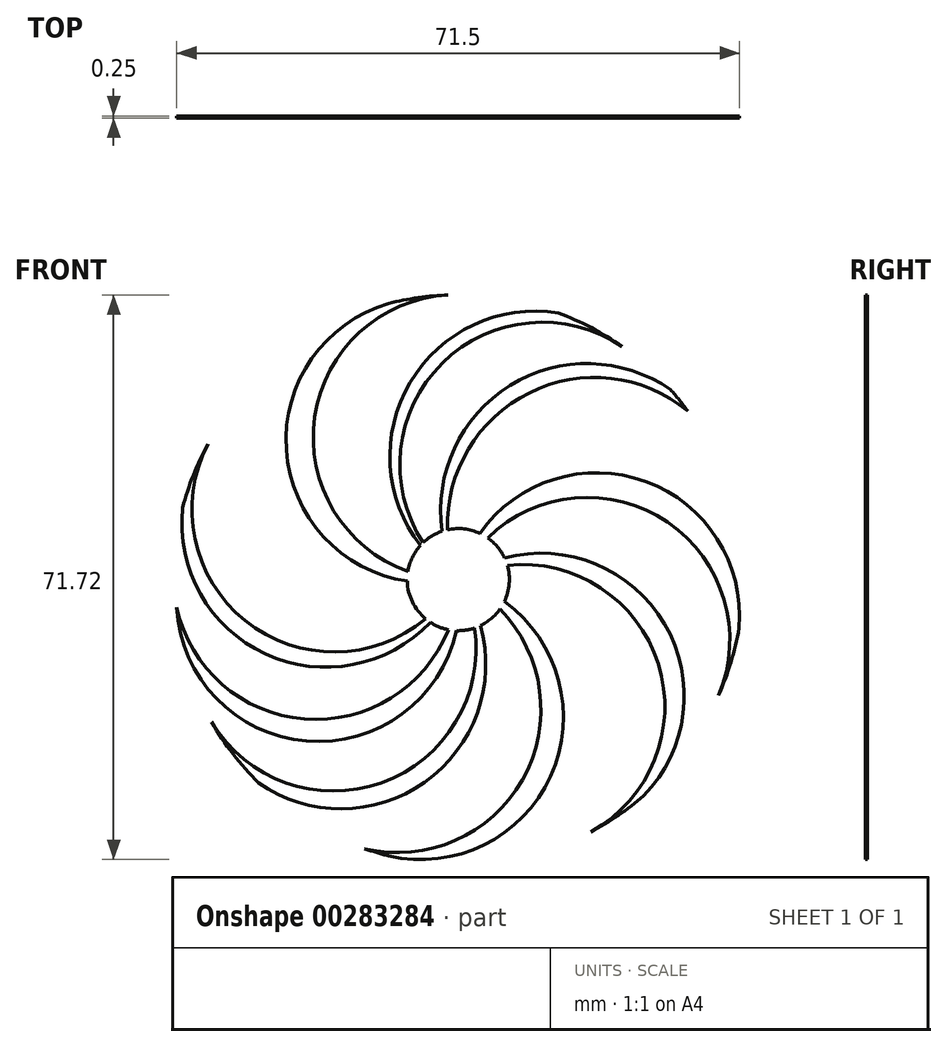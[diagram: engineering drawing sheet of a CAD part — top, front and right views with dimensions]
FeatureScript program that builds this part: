
annotation { "Feature Type Name" : "Feature", "Feature Type Description" : "" }
export const myFeature = defineFeature(function(context is Context, id is Id, definition is map)
    precondition{}
    {
        {
            var Q0;
            Q0=qCreatedBy(makeId("Front.planeOp"),FACE);
            var sketch = newSketch(context, id + "F0", { "sketchPlane" : qUnion([Q0])});
            skArc(sketch, "E0", {"start": v(0, 36.18) * mm, "mid": v(-18.42, 18.1) * mm, "end": v(0, 0) * mm});
            skArc(sketch, "E1", {"start": v(-31.34, -18.09) * mm, "mid": v(-6.79, -24.43) * mm, "end": v(0, 0) * mm});
            skArc(sketch, "E2", {"start": v(-36.18, 0) * mm, "mid": v(-18.1, -17.77) * mm, "end": v(0, 0) * mm});
            skArc(sketch, "E3", {"start": v(33.06, -14.7) * mm, "mid": v(23.75, 8.89) * mm, "end": v(0, 0) * mm});
            skArc(sketch, "E4", {"start": v(-31.81, 17.24) * mm, "mid": v(-24.37, -7) * mm, "end": v(0, 0) * mm});
            skArc(sketch, "E5", {"start": v(20.81, 29.6) * mm, "mid": v(-4.13, 25.02) * mm, "end": v(0, 0) * mm});
            skArc(sketch, "E6", {"start": v(16.86, -32.02) * mm, "mid": v(24.15, -7.73) * mm, "end": v(0, 0) * mm});
            skArc(sketch, "E7", {"start": v(-8.86, -35.08) * mm, "mid": v(12.8, -21.9) * mm, "end": v(0, 0) * mm});
            skCircle(sketch, "E8", {"center": v(0, 0) * mm, "radius": 36.18 * mm});
            skArc(sketch, "E9", {"start": v(-35.01, 9.13) * mm, "mid": v(-21.44, -10.53) * mm, "end": v(0, 0) * mm});
            skArc(sketch, "E10", {"start": v(-35.77, -3.54) * mm, "mid": v(-16.03, -20.48) * mm, "end": v(0, 0) * mm});
            skArc(sketch, "E11", {"start": v(23.55, -27.47) * mm, "mid": v(24.32, -2.98) * mm, "end": v(0, 0) * mm});
            skArc(sketch, "E12", {"start": v(-11.89, -34.18) * mm, "mid": v(9.48, -22.45) * mm, "end": v(0, 0) * mm});
            skArc(sketch, "E13", {"start": v(-25.37, -25.8) * mm, "mid": v(-1.78, -23.62) * mm, "end": v(0, 0) * mm});
            skArc(sketch, "E14", {"start": v(35.66, -6.15) * mm, "mid": v(20.65, 13.32) * mm, "end": v(0, 0) * mm});
            skArc(sketch, "E15", {"start": v(12.7, 33.88) * mm, "mid": v(-7.51, 22.14) * mm, "end": v(0, 0) * mm});
            skArc(sketch, "E16", {"start": v(26.95, 24.14) * mm, "mid": v(3.96, 22.7) * mm, "end": v(0, 0) * mm});
            skArc(sketch, "E17", {"start": v(29.14, 21.45) * mm, "mid": v(6.24, 22.05) * mm, "end": v(0, 0) * mm});
            skArc(sketch, "E18", {"start": v(-8.86, 35.08) * mm, "mid": v(-21.34, 13.27) * mm, "end": v(0, 0) * mm});
            skCircle(sketch, "E19", {"center": v(0, 0) * mm, "radius": 6.49 * mm});
            skSolve(sketch);
        }
        {
            var Q0;
            {var subQ0=sQuery(id+"F0.wireOp",EDGE,"E18");Q0=makeQuery(id+"F0.imprint","IMPRINT",FACE,{"disambiguationData":[TD([[makeQuery(id+"F0.imprint","IMPRINT",EDGE,{"derivedFrom":subQ0}),1.0]])]});}
            extrude(context, id + "F1", {"entities" : qUnion([Q0]), "depth" : 0.25 * mm});
        }
        {
            var Q0;
            {var subQ0=sQuery(id+"F0.wireOp",EDGE,"E16");Q0=makeQuery(id+"F0.imprint","IMPRINT",FACE,{"disambiguationData":[TD([[makeQuery(id+"F0.imprint","IMPRINT",EDGE,{"derivedFrom":subQ0}),1.0]])]});}
            var Q1;
            {var subQ0=sQuery(id+"F0.wireOp",EDGE,"E5");Q1=makeQuery(id+"F0.imprint","IMPRINT",FACE,{"disambiguationData":[TD([[makeQuery(id+"F0.imprint","IMPRINT",EDGE,{"derivedFrom":subQ0}),-1.0]])]});}
            var Q2;
            {var subQ0=sQuery(id+"F0.wireOp",EDGE,"E3");Q2=makeQuery(id+"F0.imprint","IMPRINT",FACE,{"disambiguationData":[TD([[makeQuery(id+"F0.imprint","IMPRINT",EDGE,{"derivedFrom":subQ0}),-1.0]])]});}
            var Q3;
            {var subQ0=sQuery(id+"F0.wireOp",EDGE,"E6");Q3=makeQuery(id+"F0.imprint","IMPRINT",FACE,{"disambiguationData":[TD([[makeQuery(id+"F0.imprint","IMPRINT",EDGE,{"derivedFrom":subQ0}),-1.0]])]});}
            var Q4;
            {var subQ0=sQuery(id+"F0.wireOp",EDGE,"E1");Q4=makeQuery(id+"F0.imprint","IMPRINT",FACE,{"disambiguationData":[TD([[makeQuery(id+"F0.imprint","IMPRINT",EDGE,{"derivedFrom":subQ0}),-1.0]])]});}
            var Q5;
            {var subQ0=sQuery(id+"F0.wireOp",EDGE,"E7");Q5=makeQuery(id+"F0.imprint","IMPRINT",FACE,{"disambiguationData":[TD([[makeQuery(id+"F0.imprint","IMPRINT",EDGE,{"derivedFrom":subQ0}),1.0]])]});}
            var Q6;
            {var subQ0=sQuery(id+"F0.wireOp",EDGE,"E10");Q6=makeQuery(id+"F0.imprint","IMPRINT",FACE,{"disambiguationData":[TD([[makeQuery(id+"F0.imprint","IMPRINT",EDGE,{"derivedFrom":subQ0}),1.0]])]});}
            var Q7;
            {var subQ0=sQuery(id+"F0.wireOp",EDGE,"E4");Q7=makeQuery(id+"F0.imprint","IMPRINT",FACE,{"disambiguationData":[TD([[makeQuery(id+"F0.imprint","IMPRINT",EDGE,{"derivedFrom":subQ0}),-1.0]])]});}
            var Q8;
            {var subQ1=sQuery(id+"F0.wireOp",EDGE,"E4");var subQ3=sQuery(id+"F0.wireOp",EDGE,"E19");var subQ4=makeQuery(id+"F0.imprint","INTERSECT",VERTEX,{"derivedFrom":[subQ1,subQ3]});Q8=makeQuery(id+"F0.imprint","IMPRINT",FACE,{"disambiguationData":[TD([[makeQuery(id+"F0.imprint","IMPRINT",EDGE,{"disambiguationData":[TD([[subQ4,1.0]])],"derivedFrom":subQ3}),1.0]])]});}
            var Q9;
            {var subQ1=sQuery(id+"F0.wireOp",EDGE,"E0");var subQ3=sQuery(id+"F0.wireOp",EDGE,"E19");var subQ4=makeQuery(id+"F0.imprint","INTERSECT",VERTEX,{"derivedFrom":[subQ1,subQ3]});Q9=makeQuery(id+"F0.imprint","IMPRINT",FACE,{"disambiguationData":[TD([[makeQuery(id+"F0.imprint","IMPRINT",EDGE,{"disambiguationData":[TD([[subQ4,1.0]])],"derivedFrom":subQ3}),1.0]])]});}
            var Q10;
            {var subQ1=sQuery(id+"F0.wireOp",EDGE,"E5");var subQ3=sQuery(id+"F0.wireOp",EDGE,"E19");var subQ4=makeQuery(id+"F0.imprint","INTERSECT",VERTEX,{"derivedFrom":[subQ1,subQ3]});Q10=makeQuery(id+"F0.imprint","IMPRINT",FACE,{"disambiguationData":[TD([[makeQuery(id+"F0.imprint","IMPRINT",EDGE,{"disambiguationData":[TD([[subQ4,1.0]])],"derivedFrom":subQ3}),1.0]])]});}
            var Q11;
            {var subQ1=sQuery(id+"F0.wireOp",EDGE,"E14");var subQ3=sQuery(id+"F0.wireOp",EDGE,"E19");var subQ4=makeQuery(id+"F0.imprint","INTERSECT",VERTEX,{"derivedFrom":[subQ1,subQ3]});Q11=makeQuery(id+"F0.imprint","IMPRINT",FACE,{"disambiguationData":[TD([[makeQuery(id+"F0.imprint","IMPRINT",EDGE,{"disambiguationData":[TD([[subQ4,-1.0]])],"derivedFrom":subQ3}),1.0]])]});}
            var Q12;
            {var subQ1=sQuery(id+"F0.wireOp",EDGE,"E3");var subQ3=sQuery(id+"F0.wireOp",EDGE,"E19");var subQ4=makeQuery(id+"F0.imprint","INTERSECT",VERTEX,{"derivedFrom":[subQ1,subQ3]});Q12=makeQuery(id+"F0.imprint","IMPRINT",FACE,{"disambiguationData":[TD([[makeQuery(id+"F0.imprint","IMPRINT",EDGE,{"disambiguationData":[TD([[subQ4,1.0]])],"derivedFrom":subQ3}),1.0]])]});}
            var Q13;
            {var subQ1=sQuery(id+"F0.wireOp",EDGE,"E6");var subQ3=sQuery(id+"F0.wireOp",EDGE,"E19");var subQ4=makeQuery(id+"F0.imprint","INTERSECT",VERTEX,{"derivedFrom":[subQ1,subQ3]});Q13=makeQuery(id+"F0.imprint","IMPRINT",FACE,{"disambiguationData":[TD([[makeQuery(id+"F0.imprint","IMPRINT",EDGE,{"disambiguationData":[TD([[subQ4,1.0]])],"derivedFrom":subQ3}),1.0]])]});}
            var Q14;
            {var subQ1=sQuery(id+"F0.wireOp",EDGE,"E12");var subQ3=sQuery(id+"F0.wireOp",EDGE,"E19");var subQ4=makeQuery(id+"F0.imprint","INTERSECT",VERTEX,{"derivedFrom":[subQ1,subQ3]});Q14=makeQuery(id+"F0.imprint","IMPRINT",FACE,{"disambiguationData":[TD([[makeQuery(id+"F0.imprint","IMPRINT",EDGE,{"disambiguationData":[TD([[subQ4,1.0]])],"derivedFrom":subQ3}),1.0]])]});}
            var Q15;
            {var subQ1=sQuery(id+"F0.wireOp",EDGE,"E1");var subQ3=sQuery(id+"F0.wireOp",EDGE,"E19");var subQ4=makeQuery(id+"F0.imprint","INTERSECT",VERTEX,{"derivedFrom":[subQ1,subQ3]});Q15=makeQuery(id+"F0.imprint","IMPRINT",FACE,{"disambiguationData":[TD([[makeQuery(id+"F0.imprint","IMPRINT",EDGE,{"disambiguationData":[TD([[subQ4,1.0]])],"derivedFrom":subQ3}),1.0]])]});}
            var Q16;
            {var subQ1=sQuery(id+"F0.wireOp",EDGE,"E2");var subQ3=sQuery(id+"F0.wireOp",EDGE,"E19");var subQ4=makeQuery(id+"F0.imprint","INTERSECT",VERTEX,{"derivedFrom":[subQ1,subQ3]});Q16=makeQuery(id+"F0.imprint","IMPRINT",FACE,{"disambiguationData":[TD([[makeQuery(id+"F0.imprint","IMPRINT",EDGE,{"disambiguationData":[TD([[subQ4,1.0]])],"derivedFrom":subQ3}),1.0]])]});}
            var Q17;
            {var subQ0=sQuery(id+"F0.wireOp",EDGE,"E8");var subQ1=sQuery(id+"F0.wireOp",EDGE,"E4");var subQ2=makeQuery(id+"F0.imprint","INTERSECT",VERTEX,{"derivedFrom":[subQ1,subQ0]});Q17=makeQuery(id+"F0.imprint","IMPRINT",FACE,{"disambiguationData":[TD([[makeQuery(id+"F0.imprint","IMPRINT",EDGE,{"disambiguationData":[TD([[subQ2,-1.0]])],"derivedFrom":subQ1}),-1.0]])]});}
            var Q18;
            {var subQ0=sQuery(id+"F0.wireOp",EDGE,"E8");var subQ1=sQuery(id+"F0.wireOp",EDGE,"E0");var subQ2=makeQuery(id+"F0.imprint","INTERSECT",VERTEX,{"disambiguationData":[OD(1.0)],"derivedFrom":[subQ1,subQ0]});Q18=makeQuery(id+"F0.imprint","IMPRINT",FACE,{"disambiguationData":[TD([[makeQuery(id+"F0.imprint","IMPRINT",EDGE,{"disambiguationData":[TD([[subQ2,-1.0]])],"derivedFrom":subQ1}),-1.0]])]});}
            var Q19;
            {var subQ0=sQuery(id+"F0.wireOp",EDGE,"E8");var subQ1=sQuery(id+"F0.wireOp",EDGE,"E5");var subQ2=makeQuery(id+"F0.imprint","INTERSECT",VERTEX,{"derivedFrom":[subQ1,subQ0]});Q19=makeQuery(id+"F0.imprint","IMPRINT",FACE,{"disambiguationData":[TD([[makeQuery(id+"F0.imprint","IMPRINT",EDGE,{"disambiguationData":[TD([[subQ2,-1.0]])],"derivedFrom":subQ1}),-1.0]])]});}
            var Q20;
            {var subQ0=sQuery(id+"F0.wireOp",EDGE,"E16");var subQ1=sQuery(id+"F0.wireOp",EDGE,"E8");var subQ2=makeQuery(id+"F0.imprint","INTERSECT",VERTEX,{"derivedFrom":[subQ1,subQ0]});Q20=makeQuery(id+"F0.imprint","IMPRINT",FACE,{"disambiguationData":[TD([[makeQuery(id+"F0.imprint","IMPRINT",EDGE,{"disambiguationData":[TD([[subQ2,1.0]])],"derivedFrom":subQ1}),1.0]])]});}
            var Q21;
            {var subQ0=sQuery(id+"F0.wireOp",EDGE,"E8");var subQ1=sQuery(id+"F0.wireOp",EDGE,"E3");var subQ2=makeQuery(id+"F0.imprint","INTERSECT",VERTEX,{"derivedFrom":[subQ1,subQ0]});Q21=makeQuery(id+"F0.imprint","IMPRINT",FACE,{"disambiguationData":[TD([[makeQuery(id+"F0.imprint","IMPRINT",EDGE,{"disambiguationData":[TD([[subQ2,-1.0]])],"derivedFrom":subQ1}),-1.0]])]});}
            var Q22;
            {var subQ0=sQuery(id+"F0.wireOp",EDGE,"E8");var subQ1=sQuery(id+"F0.wireOp",EDGE,"E6");var subQ2=makeQuery(id+"F0.imprint","INTERSECT",VERTEX,{"derivedFrom":[subQ1,subQ0]});Q22=makeQuery(id+"F0.imprint","IMPRINT",FACE,{"disambiguationData":[TD([[makeQuery(id+"F0.imprint","IMPRINT",EDGE,{"disambiguationData":[TD([[subQ2,-1.0]])],"derivedFrom":subQ1}),-1.0]])]});}
            var Q23;
            {var subQ0=sQuery(id+"F0.wireOp",EDGE,"E8");var subQ1=sQuery(id+"F0.wireOp",EDGE,"E7");var subQ2=makeQuery(id+"F0.imprint","INTERSECT",VERTEX,{"derivedFrom":[subQ1,subQ0]});Q23=makeQuery(id+"F0.imprint","IMPRINT",FACE,{"disambiguationData":[TD([[makeQuery(id+"F0.imprint","IMPRINT",EDGE,{"disambiguationData":[TD([[subQ2,-1.0]])],"derivedFrom":subQ1}),1.0]])]});}
            var Q24;
            {var subQ0=sQuery(id+"F0.wireOp",EDGE,"E8");var subQ1=sQuery(id+"F0.wireOp",EDGE,"E1");var subQ2=makeQuery(id+"F0.imprint","INTERSECT",VERTEX,{"derivedFrom":[subQ1,subQ0]});Q24=makeQuery(id+"F0.imprint","IMPRINT",FACE,{"disambiguationData":[TD([[makeQuery(id+"F0.imprint","IMPRINT",EDGE,{"disambiguationData":[TD([[subQ2,-1.0]])],"derivedFrom":subQ1}),-1.0]])]});}
            extrude(context, id + "F2", {"entities" : qUnion([Q0, Q1, Q2, Q3, Q4, Q5, Q6, Q7, Q8, Q9, Q10, Q11, Q12, Q13, Q14, Q15, Q16, Q17, Q18, Q19, Q20, Q21, Q22, Q23, Q24]), "operationType" : NewBodyOperationType.ADD, "depth" : 0.25 * mm});
        }
    });
